# Revit family: Gira_283426
name_source: partatom
category: Electrical Fixtures
revit_build: Autodesk Revit 2017 (Build: 20160225_1515(x64)
units: mm (PartAtom-declared; Revit-internal decimal feet)

## family parameters
Cut with Voids When Loaded = No
Host = Face
Maintain Annotation Orientation = Yes
Part Type = Normal
Room Calculation Point = No
Round Connector Dimension = Use Diameter
Shared = No

## types (1)
- Rocker sw. BS 20 AX CB 2-p ctrl.l. System 55 c.alum.
    Assembly arrangement = Basic element with central cover plate
    Available = No
    BIM (1) = https://media.stage.bim.site und Tasten.rfa?public/gira/36a6b08/Sys55_Komplettgerät_Schalten und Tasten.rfa
    Category = Switch
    Colour = Aluminium
    Connection type = Screwed terminal
    Data sheet (1) = https://katalog.gira.de
    Default Elevation = 1219 mm
    Description = Rock.sw.BS20AX CB 2-p ctrl.l Sys55 CAl,British Standard rocker switch (BS EN 60669-1) 20 AX 250 V~ with rocker and control light ,System 55, Support ring 71 x 71 mm, circuit breaker 2-pole,colour aluminium,Features:,- With screw terminals.,,Notes :,- For screw mounting only.
    Function lighting = Illuminated (on)
    GTIN = 4010337078838
    HAN = 283426
    Halogen free = Yes
    HeinzeBIM = https://bimportal.heinze.de
    Illumination = Yes
    Label space/information surface = No
    Manufacturer = Gira
    Manufacturer URL = https://www.gira.de
    Material = Plastic
    Material quality = Thermoplastic
    Method of operation = Rocker/button
    Mounting method = Flush mounted (plaster)
    Name = Rocker sw. BS 20 AX CB 2-p ctrl.l. System 55 c.alum.
    Nominal voltage = 250
    Number of modules (module system) = 1
    Number of rockers = 1
    Push button switch = No
    Rated current = 20
    Suitable for degree of protection (IP) = IP20
    Surface protection = Other
    Type of fastening = Screw mounting
    Type of lighting = Other
    URL = http://katalog.gira.de
    Washing machine switch = No
    Wiring system = 2-pole switch
    With mounting plate = No

## geometry (parser evidence)
native form markers: Sweep x5
no freeform markers — native parametric forms only
